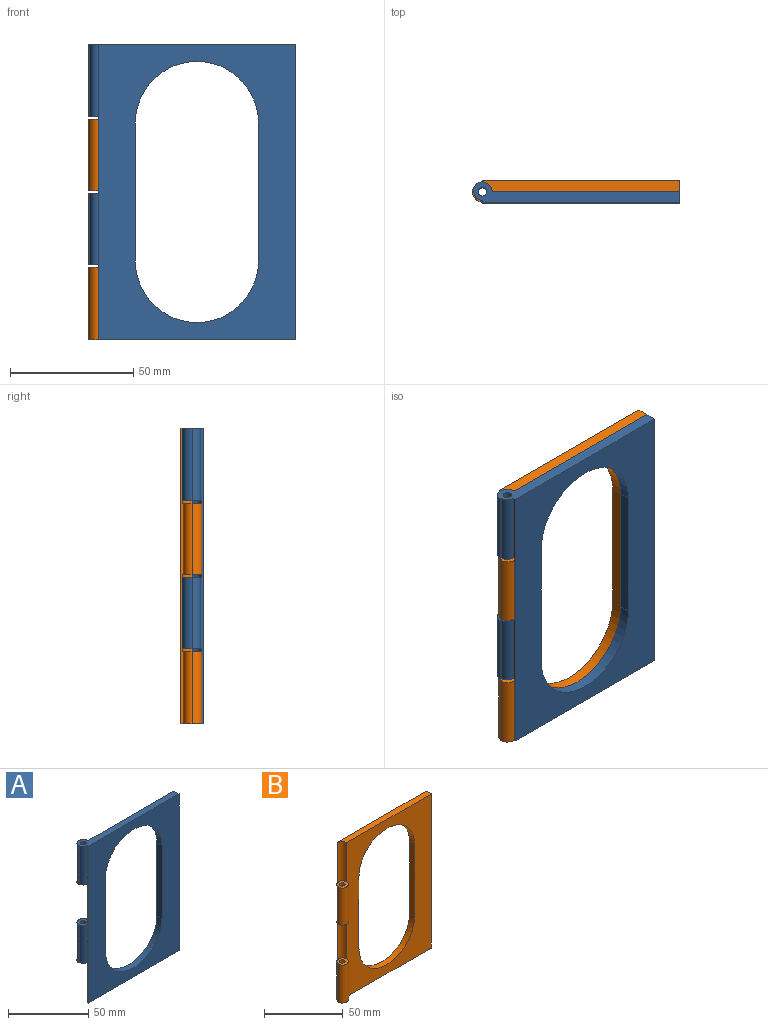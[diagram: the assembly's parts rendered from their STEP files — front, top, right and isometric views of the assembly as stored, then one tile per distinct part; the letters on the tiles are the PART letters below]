
ASSEMBLY  parts=2 mates=1
PART A: 23 faces, bbox 84x8.5x120 mm
  f0: plane 120x1mm, normal (-1,0,0), area 89.2mm2, adj f1,f4,f5,f7,f8,f9,f11,f15
  f1: cylinder r=3.5mm len=29mm, axis (0,0,1), area 159.4mm2, adj f0,f3,f17,f18
  f2: cylinder r=1.75mm len=29mm, axis (0,0,1), area 318.9mm2, adj f17,f18
  f3: plane 29x0.5mm, normal (0,-1,0), area 14.5mm2, adj f1,f16,f17,f18
  f4: cylinder r=4mm len=30.5mm, axis (0,0,1), area 191.6mm2, adj f0,f8,f10,f17
  f5: cylinder r=4mm len=31mm, axis (0,0,1), area 194.8mm2, adj f0,f10,f15,f18
  f6: plane 120x4.5mm, normal (1,0,0), area 540mm2, adj f7,f8,f9,f10
  f7: plane 84x8.5mm, normal (0,0,1), area 385.1mm2, adj f0,f6,f9,f10,f11,f12,f13,f14
  f8: plane 80x4.5mm, normal (0,0,-1), area 347.4mm2, adj f0,f4,f6,f9,f10
  f9: plane 120x80mm, normal (0,-1,0), area 4836.5mm2, adj f0,f6,f7,f8,f19,f20,f21,f22
  f10: plane 120x76mm, normal (0,1,0), area 4356.5mm2, adj f4,f5,f6,f7,f8,f12,f16,f19
  f11: cylinder r=3.5mm len=29.5mm, axis (0,0,-1), area 162.2mm2, adj f0,f7,f14,f15
  f12: cylinder r=4mm len=29.5mm, axis (0,0,-1), area 370.7mm2, adj f7,f10,f14,f15
  f13: cylinder r=1.75mm len=29.5mm, axis (0,0,-1), area 324.4mm2, adj f7,f15
  f14: plane 29.5x0.5mm, normal (0,-1,0), area 14.8mm2, adj f7,f11,f12,f15
  f15: plane 8x8mm, normal (0,0,-1), area 37.7mm2, adj f0,f5,f11,f12,f13,f14
  f16: cylinder r=4mm len=29mm, axis (0,0,1), area 364.4mm2, adj f3,f10,f17,f18
  f17: plane 8x8mm, normal (0,0,-1), area 37.7mm2, adj f0,f1,f2,f3,f4,f16
  f18: plane 8x8mm, normal (0,0,1), area 37.7mm2, adj f0,f1,f2,f3,f5,f16
  f19: plane 56x4.5mm, normal (-1,0,0), area 252mm2, adj f9,f10,f20,f22
  f20: cylinder r=25mm len=50mm, axis (0,-1,0), area 353.4mm2, adj f9,f10,f19,f21
  f21: plane 56x4.5mm, normal (1,0,0), area 252mm2, adj f9,f10,f20,f22
  f22: cylinder r=25mm len=50mm, axis (0,-1,0), area 353.4mm2, adj f9,f10,f19,f21
PART B: 23 faces, bbox 84x8.5x120 mm
  f0: plane 120x1mm, normal (-1,0,0), area 89.2mm2, adj f1,f2,f6,f7,f8,f10,f12,f14
  f1: cylinder r=4mm len=31mm, axis (0,0,1), area 194.8mm2, adj f0,f9,f12,f18
  f2: cylinder r=3.5mm len=29.5mm, axis (0,0,1), area 162.2mm2, adj f0,f3,f6,f12
  f3: plane 29.5x0.5mm, normal (0,1,0), area 14.8mm2, adj f2,f6,f11,f12
  f4: cylinder r=1.75mm len=29.5mm, axis (0,0,1), area 324.4mm2, adj f6,f12
  f5: plane 120x4.5mm, normal (1,0,0), area 540mm2, adj f6,f7,f8,f9
  f6: plane 84x8.5mm, normal (0,0,-1), area 385.1mm2, adj f0,f2,f3,f4,f5,f8,f9,f11
  f7: plane 80x4.5mm, normal (0,0,1), area 347.4mm2, adj f0,f5,f8,f9,f10
  f8: plane 120x80mm, normal (0,1,0), area 4836.5mm2, adj f0,f5,f6,f7,f19,f20,f21,f22
  f9: plane 120x76mm, normal (0,-1,0), area 4356.5mm2, adj f1,f5,f6,f7,f10,f11,f13,f19
  f10: cylinder r=4mm len=30.5mm, axis (0,0,1), area 191.6mm2, adj f0,f7,f9,f17
  f11: cylinder r=4mm len=29.5mm, axis (0,0,1), area 370.7mm2, adj f3,f6,f9,f12
  f12: plane 8x8mm, normal (0,0,1), area 37.7mm2, adj f0,f1,f2,f3,f4,f11
  f13: cylinder r=4mm len=29mm, axis (0,0,-1), area 364.4mm2, adj f9,f15,f17,f18
  f14: cylinder r=3.5mm len=29mm, axis (0,0,-1), area 159.4mm2, adj f0,f15,f17,f18
  f15: plane 29x0.5mm, normal (0,1,0), area 14.5mm2, adj f13,f14,f17,f18
  f16: cylinder r=1.75mm len=29mm, axis (0,0,-1), area 318.9mm2, adj f17,f18
  f17: plane 8x8mm, normal (0,0,1), area 37.7mm2, adj f0,f10,f13,f14,f15,f16
  f18: plane 8x8mm, normal (0,0,-1), area 37.7mm2, adj f0,f1,f13,f14,f15,f16
  f19: plane 56x4.5mm, normal (-1,0,0), area 252mm2, adj f8,f9,f20,f22
  f20: cylinder r=25mm len=50mm, axis (0,-1,0), area 353.4mm2, adj f8,f9,f19,f21
  f21: plane 56x4.5mm, normal (1,0,0), area 252mm2, adj f8,f9,f20,f22
  f22: cylinder r=25mm len=50mm, axis (0,-1,0), area 353.4mm2, adj f8,f9,f19,f21
PLACE A t=(-26.26,-23.23,1.42)mm
PLACE B t=(-26.26,-23.23,1.42)mm
MATE revolute A.f1 <-> B.f1  axis (0,0,-1) through (-66.26,-23.23,31.92)mm
